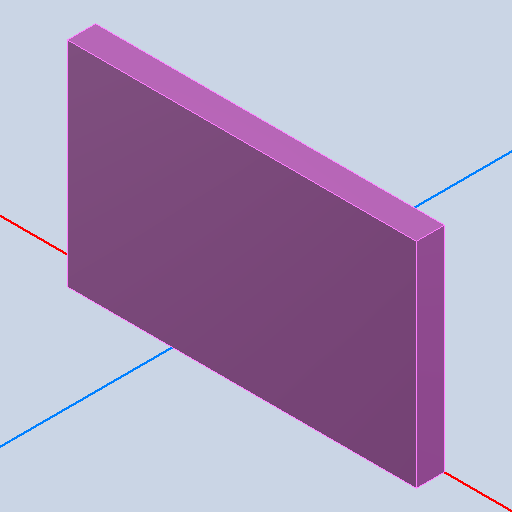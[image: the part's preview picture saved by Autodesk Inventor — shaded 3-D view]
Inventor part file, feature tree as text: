
AUTODESK INVENTOR PART (.ipt)
format: ipt  version: 2022 (Build 260153000, 153)  size: 92,160 bytes
history: native  units: mm
features: other x2, extrude x1
ambient origin geometry x8: Origin, YZ Plane, XZ Plane, XY Plane, X Axis, Y Axis, Z Axis, Center Point
bodies: Body1 (feature_tree)
feature tree (3):
  other  "Твердое тело1"
  extrude  "Выдавливание1"  Depth=1.0mm TaperAngle=0.0deg
  other  "SCREWTERMINAL-5MM-2, J2_SCREWTERMINAL-5MM-2_17"
